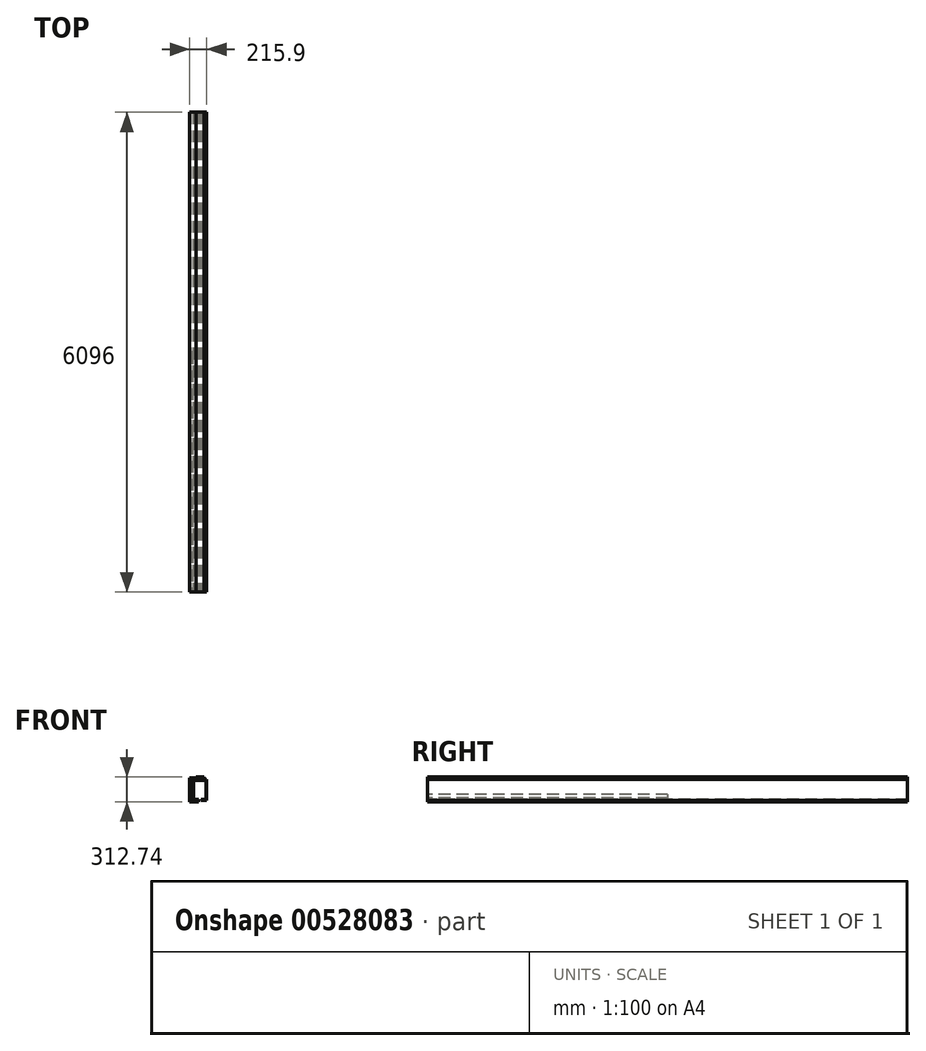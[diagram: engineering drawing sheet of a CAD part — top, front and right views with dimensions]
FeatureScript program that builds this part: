
annotation { "Feature Type Name" : "Feature", "Feature Type Description" : "" }
export const myFeature = defineFeature(function(context is Context, id is Id, definition is map)
    precondition{}
    {
        {
            var Q0;
            Q0=qCreatedBy(makeId("Front.planeOp"),FACE);
            var sketch = newSketch(context, id + "F0", { "sketchPlane" : qUnion([Q0])});
            skLineSegment(sketch, "E0", {"start": v(-3.17, 0) * mm, "end": v(-127, 0) * mm});
            skLineSegment(sketch, "E1", {"start": v(-127, 0) * mm, "end": v(-127, -304.8) * mm});
            skLineSegment(sketch, "E2", {"start": v(-127, -304.8) * mm, "end": v(-12.7, -304.8) * mm});
            skLineSegment(sketch, "E3.0", {"start": v(-101.6, -292.1) * mm, "end": v(-12.7, -292.1) * mm});
            skLineSegment(sketch, "E3.1", {"start": v(-114.3, -25.4) * mm, "end": v(-114.3, -279.4) * mm});
            skLineSegment(sketch, "E3.2", {"start": v(-3.17, -12.7) * mm, "end": v(-101.6, -12.7) * mm});
            skLineSegment(sketch, "E4", {"start": v(-12.7, -304.8) * mm, "end": v(-12.7, -292.1) * mm});
            skLineSegment(sketch, "E5", {"start": v(0, -9.52) * mm, "end": v(0, -3.17) * mm});
            skPoint(sketch, "E6.visualSharp", {"position": v(0, -12.7) * mm});
            skArc(sketch, "E6.filletArc", {"start": v(-3.17, -12.7) * mm, "mid": v(-0.93, -11.77) * mm, "end": v(0, -9.52) * mm});
            skPoint(sketch, "E7.visualSharp", {"position": v(0, 0) * mm});
            skArc(sketch, "E7.filletArc", {"start": v(0, -3.17) * mm, "mid": v(-0.93, -0.93) * mm, "end": v(-3.17, 0) * mm});
            skPoint(sketch, "E8.visualSharp", {"position": v(-114.3, -12.7) * mm});
            skArc(sketch, "E8.filletArc", {"start": v(-101.6, -12.7) * mm, "mid": v(-110.58, -16.42) * mm, "end": v(-114.3, -25.4) * mm});
            skPoint(sketch, "E9.visualSharp", {"position": v(-114.3, -292.1) * mm});
            skArc(sketch, "E9.filletArc", {"start": v(-114.3, -279.4) * mm, "mid": v(-110.58, -288.38) * mm, "end": v(-101.6, -292.1) * mm});
            skPoint(sketch, "E10.MirrorP", {"position": v(0, -12.72) * mm});
            skLineSegment(sketch, "E11.0", {"start": v(-88.9, -19.05) * mm, "end": v(-88.9, -285.75) * mm});
            skLineSegment(sketch, "E12.0", {"start": v(88.9, -19.05) * mm, "end": v(88.9, -285.75) * mm});
            skLineSegment(sketch, "E13", {"start": v(-88.9, -19.05) * mm, "end": v(88.9, -19.05) * mm});
            skLineSegment(sketch, "E14", {"start": v(-88.9, -285.75) * mm, "end": v(-12.7, -285.75) * mm});
            skLineSegment(sketch, "E15", {"start": v(88.9, -285.75) * mm, "end": v(12.7, -285.75) * mm});
            skLineSegment(sketch, "E16.0", {"start": v(-63.5, -273.05) * mm, "end": v(-12.7, -273.05) * mm});
            skLineSegment(sketch, "E16.1", {"start": v(63.5, -273.05) * mm, "end": v(12.7, -273.05) * mm});
            skLineSegment(sketch, "E16.2", {"start": v(76.2, -44.45) * mm, "end": v(76.2, -260.35) * mm});
            skLineSegment(sketch, "E16.3", {"start": v(-63.5, -31.75) * mm, "end": v(63.5, -31.75) * mm});
            skLineSegment(sketch, "E16.4", {"start": v(-76.2, -44.45) * mm, "end": v(-76.2, -260.35) * mm});
            skLineSegment(sketch, "E17", {"start": v(-12.7, -285.75) * mm, "end": v(-12.7, -273.05) * mm});
            skLineSegment(sketch, "E18", {"start": v(12.7, -285.75) * mm, "end": v(12.7, -273.05) * mm});
            skPoint(sketch, "E19.visualSharp", {"position": v(-76.2, -273.05) * mm});
            skArc(sketch, "E19.filletArc", {"start": v(-76.2, -260.35) * mm, "mid": v(-72.48, -269.33) * mm, "end": v(-63.5, -273.05) * mm});
            skPoint(sketch, "E20.visualSharp", {"position": v(-76.2, -31.75) * mm});
            skArc(sketch, "E20.filletArc", {"start": v(-63.5, -31.75) * mm, "mid": v(-72.48, -35.47) * mm, "end": v(-76.2, -44.45) * mm});
            skPoint(sketch, "E21.visualSharp", {"position": v(76.2, -31.75) * mm});
            skArc(sketch, "E21.filletArc", {"start": v(76.2, -44.45) * mm, "mid": v(72.48, -35.47) * mm, "end": v(63.5, -31.75) * mm});
            skPoint(sketch, "E22.visualSharp", {"position": v(76.2, -273.05) * mm});
            skArc(sketch, "E22.filletArc", {"start": v(63.5, -273.05) * mm, "mid": v(72.48, -269.33) * mm, "end": v(76.2, -260.35) * mm});
            skArc(sketch, "E23.0", {"start": v(-101.6, -12.95) * mm, "mid": v(-110.4, -16.6) * mm, "end": v(-114.05, -25.4) * mm});
            skLineSegment(sketch, "E24", {"start": v(-101.6, -12.95) * mm, "end": v(-90.49, -12.95) * mm});
            skLineSegment(sketch, "E25", {"start": v(-90.49, -12.95) * mm, "end": v(-90.49, -38.1) * mm});
            skLineSegment(sketch, "E26", {"start": v(-90.49, -38.1) * mm, "end": v(-92.2, -38.1) * mm});
            skLineSegment(sketch, "E27", {"start": v(-114.05, -38.1) * mm, "end": v(-114.05, -25.4) * mm});
            skArc(sketch, "E28", {"start": v(-92.2, -38.1) * mm, "mid": v(-101.6, -30.16) * mm, "end": v(-111, -38.1) * mm});
            skLineSegment(sketch, "E29.trimOffspring", {"start": v(-111, -38.1) * mm, "end": v(-114.05, -38.1) * mm});
            skLineSegment(sketch, "E30", {"start": v(-89.15, -41.27) * mm, "end": v(-89.15, -92.07) * mm});
            skLineSegment(sketch, "E31", {"start": v(-112.71, -92.07) * mm, "end": v(-89.15, -92.07) * mm});
            skLineSegment(sketch, "E32", {"start": v(-112.71, -92.07) * mm, "end": v(-112.71, -41.27) * mm});
            skLineSegment(sketch, "E33", {"start": v(-112.71, -41.27) * mm, "end": v(-111, -41.27) * mm});
            skArc(sketch, "E34", {"start": v(-92.2, -41.27) * mm, "mid": v(-101.6, -49.21) * mm, "end": v(-111, -41.27) * mm});
            skLineSegment(sketch, "E35.trimOffspring", {"start": v(-92.2, -41.27) * mm, "end": v(-89.15, -41.27) * mm});
            skLineSegment(sketch, "E36", {"start": v(-76.2, -152.4) * mm, "end": v(76.2, -152.4) * mm, "construction": true});
            skLineSegment(sketch, "E37.MirrorCS", {"start": v(-112.71, -212.72) * mm, "end": v(-89.15, -212.72) * mm});
            skLineSegment(sketch, "E38.MirrorCS", {"start": v(-89.15, -263.52) * mm, "end": v(-89.15, -212.72) * mm});
            skLineSegment(sketch, "E39.MirrorCS", {"start": v(-92.2, -263.52) * mm, "end": v(-89.15, -263.52) * mm});
            skArc(sketch, "E40.MirrorCS", {"start": v(-92.2, -263.52) * mm, "mid": v(-101.6, -255.59) * mm, "end": v(-111, -263.52) * mm});
            skLineSegment(sketch, "E41.MirrorCS", {"start": v(-112.71, -263.52) * mm, "end": v(-111, -263.52) * mm});
            skLineSegment(sketch, "E42.MirrorCS", {"start": v(-112.71, -212.72) * mm, "end": v(-112.71, -263.52) * mm});
            skArc(sketch, "E43.MirrorCS", {"start": v(-92.2, -266.7) * mm, "mid": v(-101.6, -274.64) * mm, "end": v(-111, -266.7) * mm});
            skLineSegment(sketch, "E44.MirrorCS", {"start": v(-111, -266.7) * mm, "end": v(-114.05, -266.7) * mm});
            skLineSegment(sketch, "E45.MirrorCS", {"start": v(-114.05, -266.7) * mm, "end": v(-114.05, -279.4) * mm});
            skArc(sketch, "E46.MirrorCS", {"start": v(-101.6, -291.85) * mm, "mid": v(-110.4, -288.2) * mm, "end": v(-114.05, -279.4) * mm});
            skLineSegment(sketch, "E47.MirrorCS", {"start": v(-101.6, -291.85) * mm, "end": v(-90.49, -291.85) * mm});
            skLineSegment(sketch, "E48.MirrorCS", {"start": v(-90.49, -291.85) * mm, "end": v(-90.49, -266.7) * mm});
            skLineSegment(sketch, "E49.MirrorCS", {"start": v(-90.49, -266.7) * mm, "end": v(-92.2, -266.7) * mm});
            skLineSegment(sketch, "E50.bottom", {"start": v(-50.8, 1.59) * mm, "end": v(50.8, 1.59) * mm});
            skLineSegment(sketch, "E50.top", {"start": v(-50.8, 7.94) * mm, "end": v(50.8, 7.94) * mm});
            skLineSegment(sketch, "E50.left", {"start": v(-50.8, 1.59) * mm, "end": v(-50.8, 7.94) * mm});
            skLineSegment(sketch, "E50.right", {"start": v(50.8, 1.59) * mm, "end": v(50.8, 7.94) * mm});
            skPoint(sketch, "E51", {"position": v(-89.15, -212.72) * mm});
            skPoint(sketch, "E52", {"position": v(-88.9, -212.72) * mm});
            skSolve(sketch);
        }
        {
            var Q0;
            Q0=makeQuery(id+"F0.imprint","IMPRINT",FACE,{"disambiguationData":[TD([[makeQuery(id+"F0.imprint","IMPRINT",EDGE,{"derivedFrom":sQuery(id+"F0.wireOp",EDGE,"E0")}),1.0]])]});
            var Q1;
            Q1=makeQuery(id+"F0.imprint","IMPRINT",FACE,{"disambiguationData":[TD([[makeQuery(id+"F0.imprint","IMPRINT",EDGE,{"derivedFrom":sQuery(id+"F0.wireOp",EDGE,"E11.0")}),1.0]])]});
            var Q2;
            Q2=makeQuery(id+"F0.imprint","IMPRINT",FACE,{"disambiguationData":[TD([[makeQuery(id+"F0.imprint","IMPRINT",EDGE,{"derivedFrom":sQuery(id+"F0.wireOp",EDGE,"E43.MirrorCS")}),1.0]])]});
            var Q3;
            Q3=makeQuery(id+"F0.imprint","IMPRINT",FACE,{"disambiguationData":[TD([[makeQuery(id+"F0.imprint","IMPRINT",EDGE,{"derivedFrom":sQuery(id+"F0.wireOp",EDGE,"E50.bottom")}),1.0]])]});
            extrude(context, id + "F1", {"entities" : qUnion([Q0, Q1, Q2, Q3]), "oppositeDirection" : true, "depth" : 6096 * mm, "offsetDistance" : 25.4 * mm});
        }
        {
            var Q0;
            Q0=makeQuery(id+"F0.imprint","IMPRINT",FACE,{"disambiguationData":[TD([[makeQuery(id+"F0.imprint","IMPRINT",EDGE,{"derivedFrom":sQuery(id+"F0.wireOp",EDGE,"E37.MirrorCS")}),-1.0]])]});
            extrude(context, id + "F2", {"entities" : qUnion([Q0]), "oppositeDirection" : true, "depth" : 3048 * mm, "offsetDistance" : 25.4 * mm});
        }
    });
